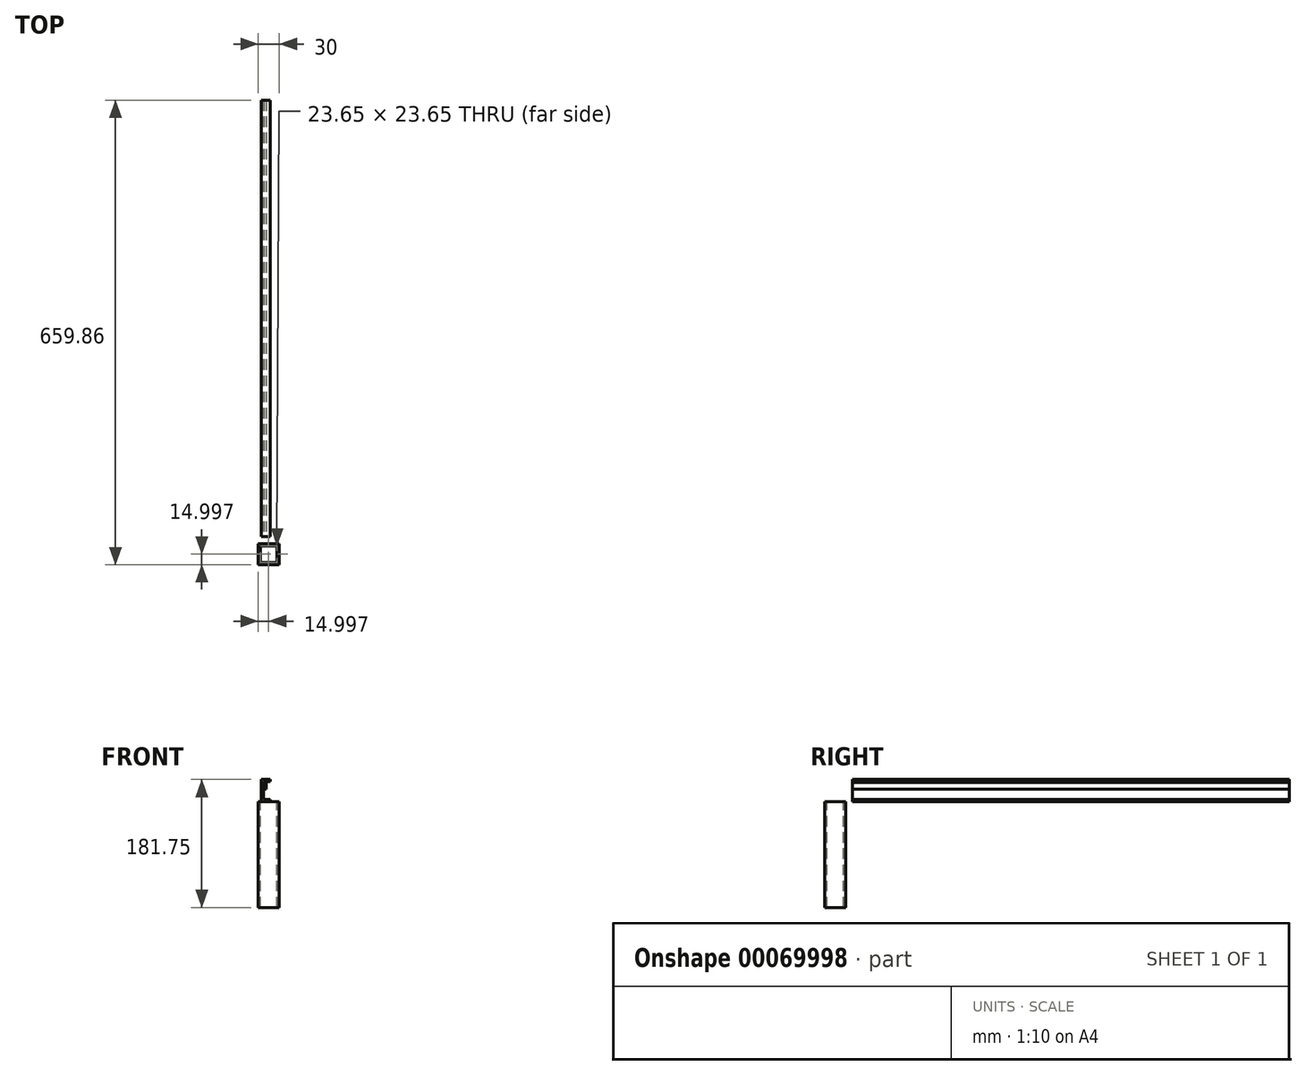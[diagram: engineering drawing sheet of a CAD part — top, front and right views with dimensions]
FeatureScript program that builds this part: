
annotation { "Feature Type Name" : "Feature", "Feature Type Description" : "" }
export const myFeature = defineFeature(function(context is Context, id is Id, definition is map)
    precondition{}
    {
        {
            var Q0;
            Q0=qCreatedBy(makeId("Front.planeOp"),FACE);
            var sketch = newSketch(context, id + "F0", { "sketchPlane" : qUnion([Q0])});
            skLineSegment(sketch, "E0.bottom", {"start": v(-6.35, 31.75) * mm, "end": v(6.35, 31.75) * mm});
            skLineSegment(sketch, "E0.top", {"start": v(-6.35, 0) * mm, "end": v(6.35, 0) * mm});
            skLineSegment(sketch, "E0.left", {"start": v(-6.35, 31.75) * mm, "end": v(-6.35, 0) * mm});
            skLineSegment(sketch, "E0.right", {"start": v(6.35, 31.75) * mm, "end": v(6.35, 28.57) * mm});
            skLineSegment(sketch, "E1.1", {"start": v(-3.18, 28.57) * mm, "end": v(6.35, 28.57) * mm});
            skLineSegment(sketch, "E1.2", {"start": v(-3.18, 28.57) * mm, "end": v(-3.18, 3.18) * mm});
            skLineSegment(sketch, "E1.3", {"start": v(-3.18, 3.18) * mm, "end": v(6.35, 3.18) * mm});
            skLineSegment(sketch, "E2.trimOffspring", {"start": v(6.35, 3.18) * mm, "end": v(6.35, 0) * mm});
            skSolve(sketch);
        }
        {
            var Q0;
            Q0=qCreatedBy(makeId("Front.planeOp"),FACE);
            var sketch = newSketch(context, id + "F1", { "sketchPlane" : qUnion([Q0])});
            skLineSegment(sketch, "E3.bottom", {"start": v(-2.36, 27.85) * mm, "end": v(0.82, 27.85) * mm});
            skLineSegment(sketch, "E3.top", {"start": v(-2.36, 17.92) * mm, "end": v(0.82, 17.92) * mm});
            skLineSegment(sketch, "E3.left", {"start": v(-2.36, 27.85) * mm, "end": v(-2.36, 17.92) * mm});
            skLineSegment(sketch, "E3.right", {"start": v(0.82, 27.85) * mm, "end": v(0.82, 17.92) * mm});
            skSolve(sketch);
        }
        {
            var Q0;
            Q0 = qSketchRegion(id + "F0", true);
            extrude(context, id + "F2", {"entities" : qUnion([Q0]), "oppositeDirection" : true, "depth" : 620 * mm});
        }
        {
            var Q0;
            Q0 = qSketchRegion(id + "F1", true);
            extrude(context, id + "F3", {"entities" : qUnion([Q0]), "oppositeDirection" : true, "depth" : 620 * mm});
        }
        {
            var Q0;
            Q0=qCreatedBy(makeId("Top.planeOp"),FACE);
            var sketch = newSketch(context, id + "F4", { "sketchPlane" : qUnion([Q0])});
            skLineSegment(sketch, "E4.bottom", {"start": v(-10.8, -9.86) * mm, "end": v(19.2, -9.86) * mm});
            skLineSegment(sketch, "E4.top", {"start": v(-10.8, -39.86) * mm, "end": v(19.2, -39.86) * mm});
            skLineSegment(sketch, "E4.left", {"start": v(-10.8, -9.86) * mm, "end": v(-10.8, -39.86) * mm});
            skLineSegment(sketch, "E4.right", {"start": v(19.2, -9.86) * mm, "end": v(19.2, -39.86) * mm});
            skLineSegment(sketch, "E5.0", {"start": v(-7.62, -13.04) * mm, "end": v(16.03, -13.04) * mm});
            skLineSegment(sketch, "E5.1", {"start": v(-7.62, -13.04) * mm, "end": v(-7.62, -36.69) * mm});
            skLineSegment(sketch, "E5.2", {"start": v(-7.62, -36.69) * mm, "end": v(16.03, -36.69) * mm});
            skLineSegment(sketch, "E5.3", {"start": v(16.03, -13.04) * mm, "end": v(16.03, -36.69) * mm});
            skSolve(sketch);
        }
        {
            var Q0;
            Q0 = qSketchRegion(id + "F4", true);
            extrude(context, id + "F5", {"entities" : qUnion([Q0]), "oppositeDirection" : true, "depth" : 150 * mm});
        }
    });
